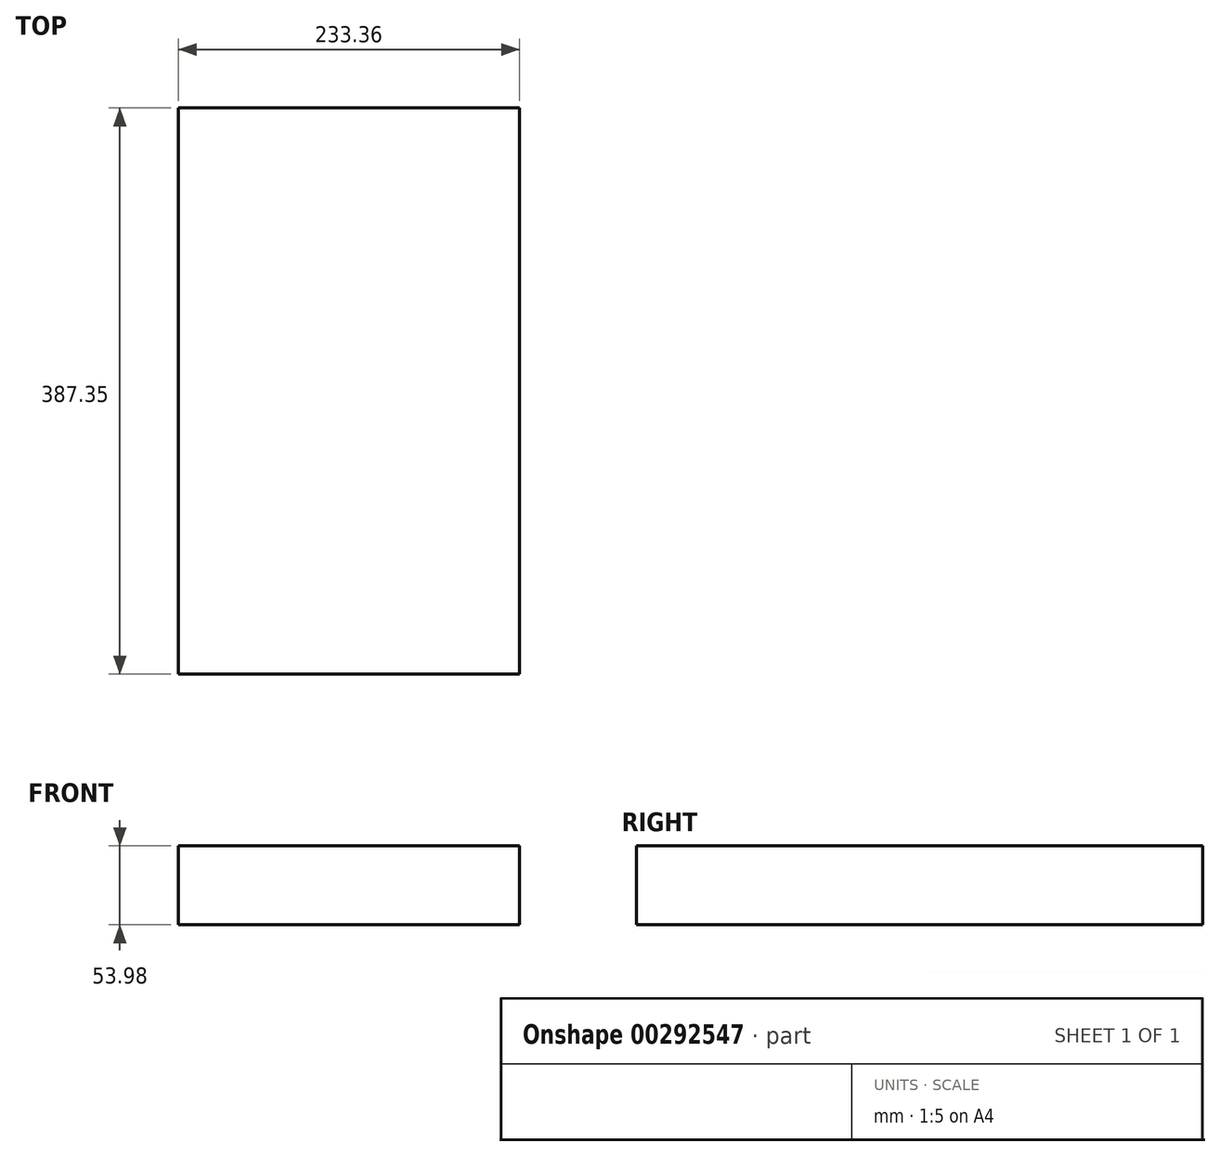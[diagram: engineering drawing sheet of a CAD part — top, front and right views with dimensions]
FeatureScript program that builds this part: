
annotation { "Feature Type Name" : "Feature", "Feature Type Description" : "" }
export const myFeature = defineFeature(function(context is Context, id is Id, definition is map)
    precondition{}
    {
        {
            var Q0;
            Q0=qCreatedBy(makeId("Top.planeOp"),FACE);
            var sketch = newSketch(context, id + "F0", { "sketchPlane" : qUnion([Q0])});
            skLineSegment(sketch, "E0.bottom", {"start": v(0, 0) * mm, "end": v(233.36, 0) * mm});
            skLineSegment(sketch, "E0.top", {"start": v(0, 387.35) * mm, "end": v(233.36, 387.35) * mm});
            skLineSegment(sketch, "E0.left", {"start": v(0, 0) * mm, "end": v(0, 387.35) * mm});
            skLineSegment(sketch, "E0.right", {"start": v(233.36, 0) * mm, "end": v(233.36, 387.35) * mm});
            skSolve(sketch);
        }
        {
            var Q0;
            Q0 = qSketchRegion(id + "F0", true);
            extrude(context, id + "F1", {"entities" : qUnion([Q0]), "depth" : 53.97 * mm});
        }
    });
